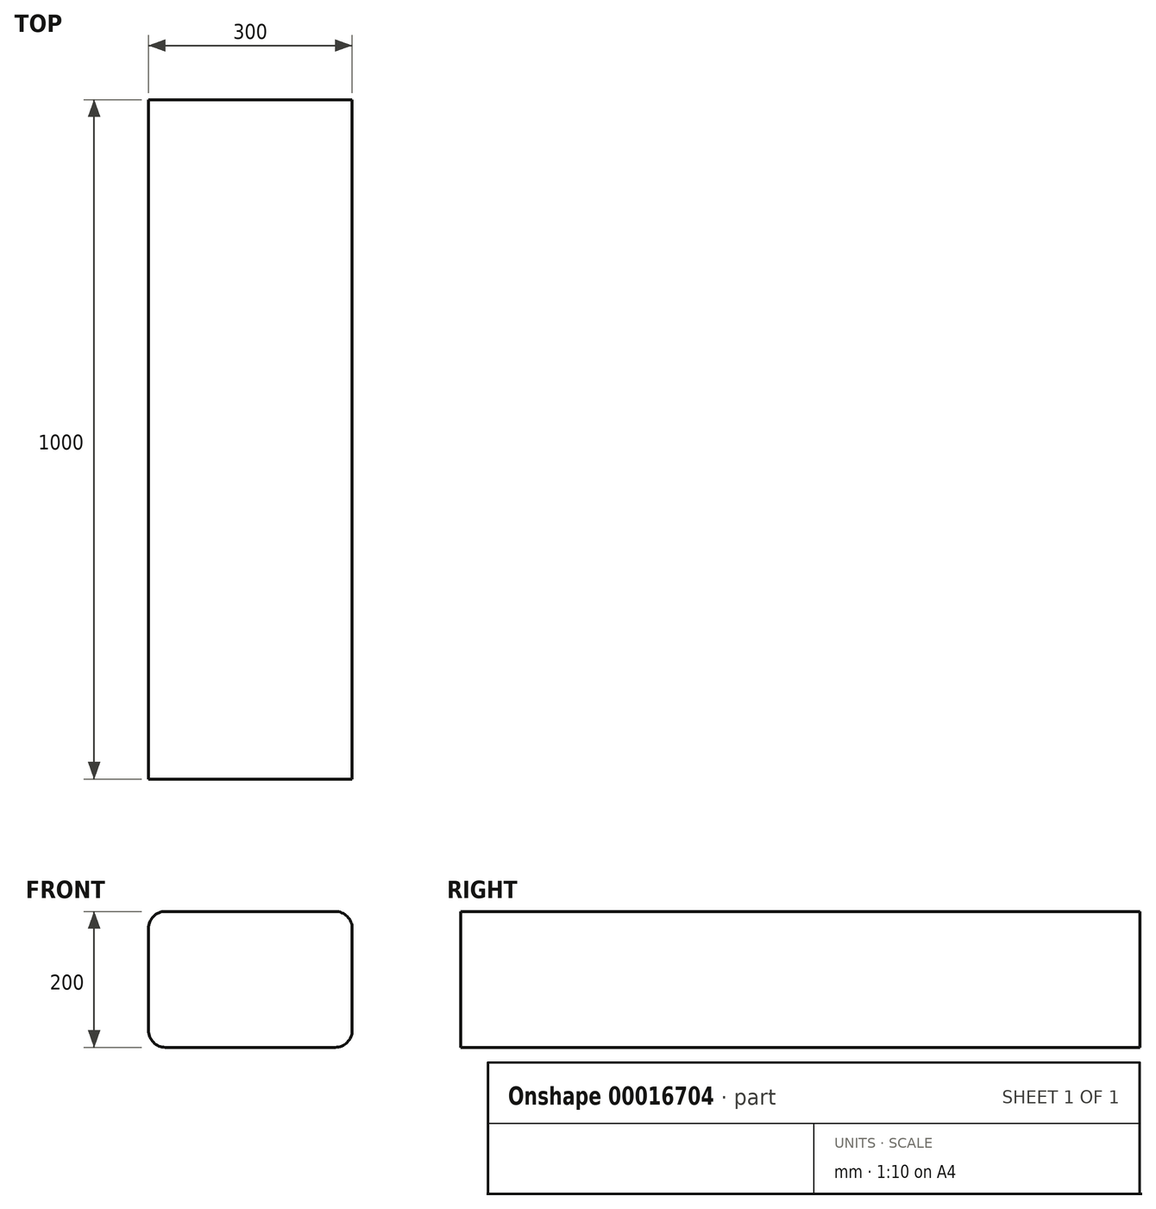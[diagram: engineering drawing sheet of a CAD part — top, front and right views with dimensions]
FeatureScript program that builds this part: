
annotation { "Feature Type Name" : "Feature", "Feature Type Description" : "" }
export const myFeature = defineFeature(function(context is Context, id is Id, definition is map)
    precondition{}
    {
        {
            var Q0;
            Q0=qCreatedBy(makeId("Front.planeOp"),FACE);
            var sketch = newSketch(context, id + "F0", { "sketchPlane" : qUnion([Q0])});
            skLineSegment(sketch, "E0.bottom", {"start": v(-150, -100) * mm, "end": v(150, -100) * mm});
            skLineSegment(sketch, "E0.top", {"start": v(-150, 100) * mm, "end": v(150, 100) * mm});
            skLineSegment(sketch, "E0.left", {"start": v(-150, -100) * mm, "end": v(-150, 100) * mm});
            skLineSegment(sketch, "E0.right", {"start": v(150, -100) * mm, "end": v(150, 100) * mm});
            skSolve(sketch);
        }
        {
            var Q0;
            Q0=makeQuery(id+"F0.imprint","IMPRINT",FACE,{"disambiguationData":[TD([[makeQuery(id+"F0.imprint","IMPRINT",EDGE,{"derivedFrom":sQuery(id+"F0.wireOp",EDGE,"E0.bottom")}),1.0]])]});
            extrude(context, id + "F1", {"entities" : qUnion([Q0]), "oppositeDirection" : true, "depth" : 1000 * mm});
        }
        {
            var Q0;
            Q0=makeQuery(id+"F1.opExtrude","SWEPT_EDGE",EDGE,{"disambiguationData":[OSD([sQuery(id+"F0.wireOp",EDGE,"E0.top"),sQuery(id+"F0.wireOp",EDGE,"E0.right")])]});
            var Q1;
            Q1=makeQuery(id+"F1.opExtrude","SWEPT_EDGE",EDGE,{"disambiguationData":[OSD([sQuery(id+"F0.wireOp",EDGE,"E0.top"),sQuery(id+"F0.wireOp",EDGE,"E0.left")])]});
            var Q2;
            Q2=makeQuery(id+"F1.opExtrude","SWEPT_EDGE",EDGE,{"disambiguationData":[OSD([sQuery(id+"F0.wireOp",EDGE,"E0.bottom"),sQuery(id+"F0.wireOp",EDGE,"E0.right")])]});
            var Q3;
            Q3=makeQuery(id+"F1.opExtrude","SWEPT_EDGE",EDGE,{"disambiguationData":[OSD([sQuery(id+"F0.wireOp",EDGE,"E0.bottom"),sQuery(id+"F0.wireOp",EDGE,"E0.left")])]});
            fillet(context, id + "F2", {"entities" : qUnion([Q0, Q1, Q2, Q3]), "radius" : 25 * mm, "tangentPropagation" : true, "allowEdgeOverflow" : false});
        }
    });
